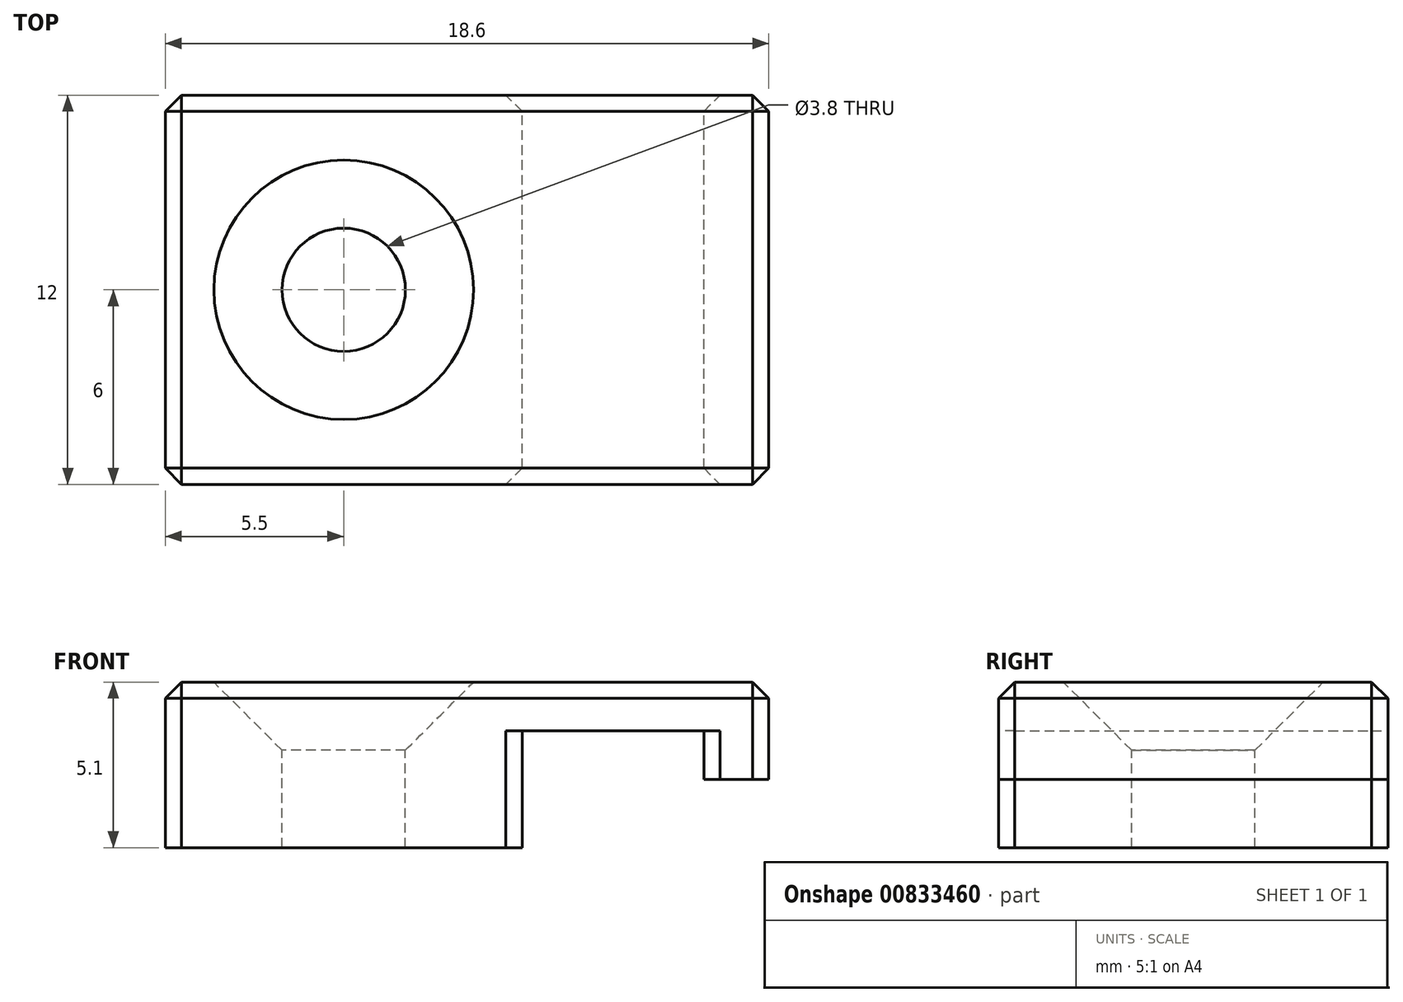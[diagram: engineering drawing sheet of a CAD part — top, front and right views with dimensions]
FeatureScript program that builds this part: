
annotation { "Feature Type Name" : "Feature", "Feature Type Description" : "" }
export const myFeature = defineFeature(function(context is Context, id is Id, definition is map)
    precondition{}
    {
        {
            var Q0;
            Q0=qCreatedBy(makeId("Front.planeOp"),FACE);
            var sketch = newSketch(context, id + "F0", { "sketchPlane" : qUnion([Q0])});
            skLineSegment(sketch, "E0", {"start": v(0, 0) * mm, "end": v(0, 3.6) * mm});
            skLineSegment(sketch, "E1", {"start": v(0, 3.6) * mm, "end": v(5.6, 3.6) * mm});
            skLineSegment(sketch, "E2", {"start": v(5.6, 3.6) * mm, "end": v(5.6, 2.1) * mm});
            skLineSegment(sketch, "E3", {"start": v(5.6, 2.1) * mm, "end": v(7.6, 2.1) * mm});
            skLineSegment(sketch, "E4", {"start": v(7.6, 2.1) * mm, "end": v(7.6, 5.1) * mm});
            skLineSegment(sketch, "E5", {"start": v(7.6, 5.1) * mm, "end": v(-11, 5.1) * mm});
            skLineSegment(sketch, "E6", {"start": v(-11, 5.1) * mm, "end": v(-11, 0) * mm});
            skLineSegment(sketch, "E7", {"start": v(-11, 0) * mm, "end": v(0, 0) * mm});
            skSolve(sketch);
        }
        {
            var Q0;
            Q0=makeQuery(id+"F0.imprint","IMPRINT",FACE,{"disambiguationData":[TD([[makeQuery(id+"F0.imprint","IMPRINT",EDGE,{"derivedFrom":sQuery(id+"F0.wireOp",EDGE,"E0")}),1.0]])]});
            extrude(context, id + "F1", {"entities" : qUnion([Q0]), "depth" : 12 * mm, "offsetDistance" : 25 * mm});
        }
        {
            var Q0;
            Q0=makeQuery(id+"F1.opExtrude","SWEPT_FACE",FACE,{"disambiguationData":[OSD([sQuery(id+"F0.wireOp",EDGE,"E7")])]});
            var sketch = newSketch(context, id + "F2", { "sketchPlane" : qUnion([Q0])});
            skLineSegment(sketch, "E8.0", {"start": v(-11, 12) * mm, "end": v(0, 12) * mm});
            skLineSegment(sketch, "E9.0", {"start": v(-11, 12) * mm, "end": v(-11, 0) * mm});
            skLineSegment(sketch, "E10.0", {"start": v(-11, 0) * mm, "end": v(0, 0) * mm});
            skLineSegment(sketch, "E11.0", {"start": v(0, 12) * mm, "end": v(0, 0) * mm});
            skLineSegment(sketch, "E12", {"start": v(-11, 12) * mm, "end": v(0, 0) * mm});
            skLineSegment(sketch, "E13", {"start": v(0, 12) * mm, "end": v(-11, 0) * mm});
            skPoint(sketch, "E14", {"position": v(-5.5, 6) * mm});
            skSolve(sketch);
        }
        {
            var Q0;
            Q0=makeQuery(id+"F1.opExtrude","SWEPT_FACE",FACE,{"disambiguationData":[OSD([sQuery(id+"F0.wireOp",EDGE,"E5")])]});
            var sketch = newSketch(context, id + "F3", { "sketchPlane" : qUnion([Q0])});
            skPoint(sketch, "E15.0", {"position": v(-5.5, -6) * mm});
            skSolve(sketch);
        }
        {
            var Q0;
            Q0=sQuery(id+"F3.wireOp",VERTEX,"E15.0");
            var Q1;
            Q1=makeQuery(id+"F1.opExtrude","SWEPT_BODY",BODY,{"disambiguationData":[OSD([sQuery(id+"F0.wireOp",EDGE,"E0"),sQuery(id+"F0.wireOp",EDGE,"E1"),sQuery(id+"F0.wireOp",EDGE,"E2"),sQuery(id+"F0.wireOp",EDGE,"E3"),sQuery(id+"F0.wireOp",EDGE,"E4"),sQuery(id+"F0.wireOp",EDGE,"E5"),sQuery(id+"F0.wireOp",EDGE,"E6"),sQuery(id+"F0.wireOp",EDGE,"E7")])]});
            hole(context, id + "F4", {"style" : HoleStyle.C_SINK, "endStyle" : HoleEndStyle.BLIND, "holeDiameter" : 3.8 * mm, "cSinkDiameter" : 8 * mm, "cSinkAngle" : 90 * degree, "majorDiameter" : 5 * mm, "holeDepth" : 40 * mm, "isTappedThrough" : true, "tappedDepth" : 100 * mm, "tapClearance" : 3, "startFromSketch" : true, "locations" : qUnion([Q0]), "scope" : qUnion([Q1])});
        }
        {
            var Q0;
            Q0=makeQuery(id+"F1.opExtrude","CAP_EDGE",EDGE,{"disambiguationData":[OSD([sQuery(id+"F0.wireOp",EDGE,"E5")])],"isStart":false});
            var Q1;
            Q1=makeQuery(id+"F1.opExtrude","SWEPT_EDGE",EDGE,{"disambiguationData":[OSD([sQuery(id+"F0.wireOp",EDGE,"E4"),sQuery(id+"F0.wireOp",EDGE,"E5")])]});
            var Q2;
            Q2=makeQuery(id+"F1.opExtrude","CAP_EDGE",EDGE,{"disambiguationData":[OSD([sQuery(id+"F0.wireOp",EDGE,"E5")])],"isStart":true});
            var Q3;
            Q3=makeQuery(id+"F1.opExtrude","SWEPT_EDGE",EDGE,{"disambiguationData":[OSD([sQuery(id+"F0.wireOp",EDGE,"E5"),sQuery(id+"F0.wireOp",EDGE,"E6")])]});
            var Q4;
            Q4=makeQuery(id+"F1.opExtrude","CAP_EDGE",EDGE,{"disambiguationData":[OSD([sQuery(id+"F0.wireOp",EDGE,"E6")])],"isStart":false});
            var Q5;
            Q5=makeQuery(id+"F1.opExtrude","CAP_EDGE",EDGE,{"disambiguationData":[OSD([sQuery(id+"F0.wireOp",EDGE,"E6")])],"isStart":true});
            var Q6;
            Q6=makeQuery(id+"F1.opExtrude","CAP_EDGE",EDGE,{"disambiguationData":[OSD([sQuery(id+"F0.wireOp",EDGE,"E4")])],"isStart":true});
            var Q7;
            Q7=makeQuery(id+"F1.opExtrude","CAP_EDGE",EDGE,{"disambiguationData":[OSD([sQuery(id+"F0.wireOp",EDGE,"E4")])],"isStart":false});
            var Q8;
            Q8=makeQuery(id+"F1.opExtrude","CAP_EDGE",EDGE,{"disambiguationData":[OSD([sQuery(id+"F0.wireOp",EDGE,"E0")])],"isStart":false});
            var Q9;
            Q9=makeQuery(id+"F1.opExtrude","CAP_EDGE",EDGE,{"disambiguationData":[OSD([sQuery(id+"F0.wireOp",EDGE,"E2")])],"isStart":false});
            var Q10;
            Q10=makeQuery(id+"F1.opExtrude","CAP_EDGE",EDGE,{"disambiguationData":[OSD([sQuery(id+"F0.wireOp",EDGE,"E0")])],"isStart":true});
            var Q11;
            Q11=makeQuery(id+"F1.opExtrude","CAP_EDGE",EDGE,{"disambiguationData":[OSD([sQuery(id+"F0.wireOp",EDGE,"E2")])],"isStart":true});
            chamfer(context, id + "F5", {"entities" : qUnion([Q0, Q1, Q2, Q3, Q4, Q5, Q6, Q7, Q8, Q9, Q10, Q11]), "width" : .5 * mm, "tangentPropagation" : true});
        }
    });
